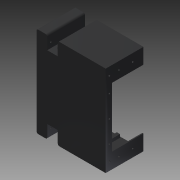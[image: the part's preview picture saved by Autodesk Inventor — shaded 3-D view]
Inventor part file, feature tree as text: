
AUTODESK INVENTOR PART (.ipt)
format: ipt  version: 2016 (Build 200138000, 138)  size: 441,856 bytes
history: native  units: mm
features: extrude x18, sketch x18, fillet x1
ambient origin geometry x8: Origin, YZ Plane, XZ Plane, XY Plane, X Axis, Y Axis, Z Axis, Center Point
bodies: Solid1 (feature_tree)
feature tree (37):
  extrude  "Extrusion1"  Depth=20.0mm
  extrude  "Extrusion2"  Depth=90.0mm
  extrude  "Extrusion3"  Depth=2.0mm
  extrude  "Extrusion4"  Depth=2.0mm
  extrude  "Extrusion5"  Depth=2.0mm
  extrude  "Extrusion6"  Depth=2.0mm
  extrude  "Extrusion7"  Depth=2.0mm
  extrude  "Extrusion8"  Depth=2.0mm
  extrude  "Extrusion9"  Depth=2.0mm
  extrude  "Extrusion10"  Depth=27.0mm
  extrude  "Extrusion11"  Depth=10.0mm TaperAngle=0.0deg
  sketch  "Sketch12"  dims[d27=5.0mm d28=3.0mm]
  extrude  "Extrusion13"  Depth=3.0mm
  extrude  "Extrusion14"  Depth=3.0mm
  extrude  "Extrusion15"  Depth=3.0mm
  extrude  "Extrusion22"  Depth=25.0mm
  extrude  "Extrusion23"  Depth=3.0mm
  extrude  "Extrusion28"  Depth=7.0mm
  extrude  "Extrusion29"  Depth=3.0mm
  fillet  "Fillet1"  Radius=4.0mm
  sketch  "Sketch1"  dims[d0=170.0mm d1=20.0mm]
  sketch  "Sketch2"  dims[d3=20.0mm d4=90.0mm]
  sketch  "Sketch3"  dims[d5=2.0mm d6=0.0mm d7=2.0mm]
  sketch  "Sketch4"  dims[d8=2.0mm d9=2.0mm]
  sketch  "Sketch5"  dims[d10=4.0mm d11=2.0mm]
  sketch  "Sketch6"  dims[d13=2.0mm d14=2.0mm]
  sketch  "Sketch7"  dims[d15=4.0mm d16=2.0mm]
  sketch  "Sketch8"  dims[d17=2.0mm d18=2.0mm]
  sketch  "Sketch9"  dims[d19=2.0mm d20=2.0mm]
  sketch  "Sketch10"  dims[d21=27.0mm d22=27.0mm]
  sketch  "Sketch11"  dims[d23=69.0mm d24=0.0mm d25=10.0mm d26=0.0mm]
  sketch  "Sketch13"  dims[d30=15.0mm d31=3.0mm]
  sketch  "Sketch14"  dims[d32=15.0mm d33=3.0mm]
  sketch  "Sketch22"  dims[d34=20.0mm d35=25.0mm]
  sketch  "Sketch23"  dims[d36=3.0mm d37=3.0mm]
  sketch  "Sketch33"  dims[d38=2.0mm d39=0.0mm d40=7.0mm]
  sketch  "Sketch34"  dims[d41=10.0mm d42=3.2mm d43=4.0mm d44=0.0mm d45=7.0mm d46=10.0mm d47=3.2mm d48=4.0mm d49=0.0mm d50=7.0mm d51=10.0mm d52=3.2mm d53=4.0mm d54=0.0mm d55=7.0mm d56=10.0mm d57=3.2mm d58=4.0mm d59=0.0mm d60=7.0mm d63=3.2mm d64=3.2mm d65=2.0mm d66=0.0mm d67=7.0mm d68=2.625mm d69=3.0mm d70=4.0mm d71=0.0mm d72=7.0mm d73=2.625mm d74=3.0mm d75=4.0mm d76=0.0mm d80=20.0mm d81=150.0mm d82=10.0mm d83=10.0mm d84=90.0mm d85=15.0mm d86=15.0mm d87=14.5mm d88=3.0mm d89=3.0mm d95=6.0mm d96=6.0mm d97=6.0mm d98=6.0mm d99=67.0mm d100=0.0mm d101=67.0mm d102=0.0mm d103=6.0mm d104=3.0mm d105=3.0mm d106=25.0mm d107=0.0mm d167=40.0mm d168=40.0mm d209=11.0mm d210=2.5mm d211=5.0mm d212=5.0mm d213=4.0mm d214=0.0mm d215=11.0mm d216=2.5mm d217=5.0mm d218=5.0mm d219=4.0mm d220=0.0mm d221=3.0mm d222=6.0mm d226=25.0mm d227=25.0mm d228=25.0mm d229=3.0mm d230=3.0mm d231=3.0mm d232=3.0mm d233=3.0mm d292=10.0mm d293=10.0mm d308=3.0mm d309=3.0mm d329=78.0mm d331=4.0mm d332=158.0mm d333=158.0mm d334=78.0mm d335=4.0mm d336=8.0mm d337=8.0mm d338=8.0mm d339=8.0mm d340=8.0mm d341=8.0mm d342=8.0mm d343=8.0mm d344=24.0mm d345=0.0mm d346=15.0mm d347=0.0mm d348=30.4mm d349=2.0mm d350=2.0mm d352=2.0mm d353=2.0mm d354=99.0mm d355=2.0mm d356=34.4mm d357=32.4mm d358=30.4mm d359=28.0mm d360=2.0mm d361=24.0mm d362=0.0mm d364=3.0mm]
